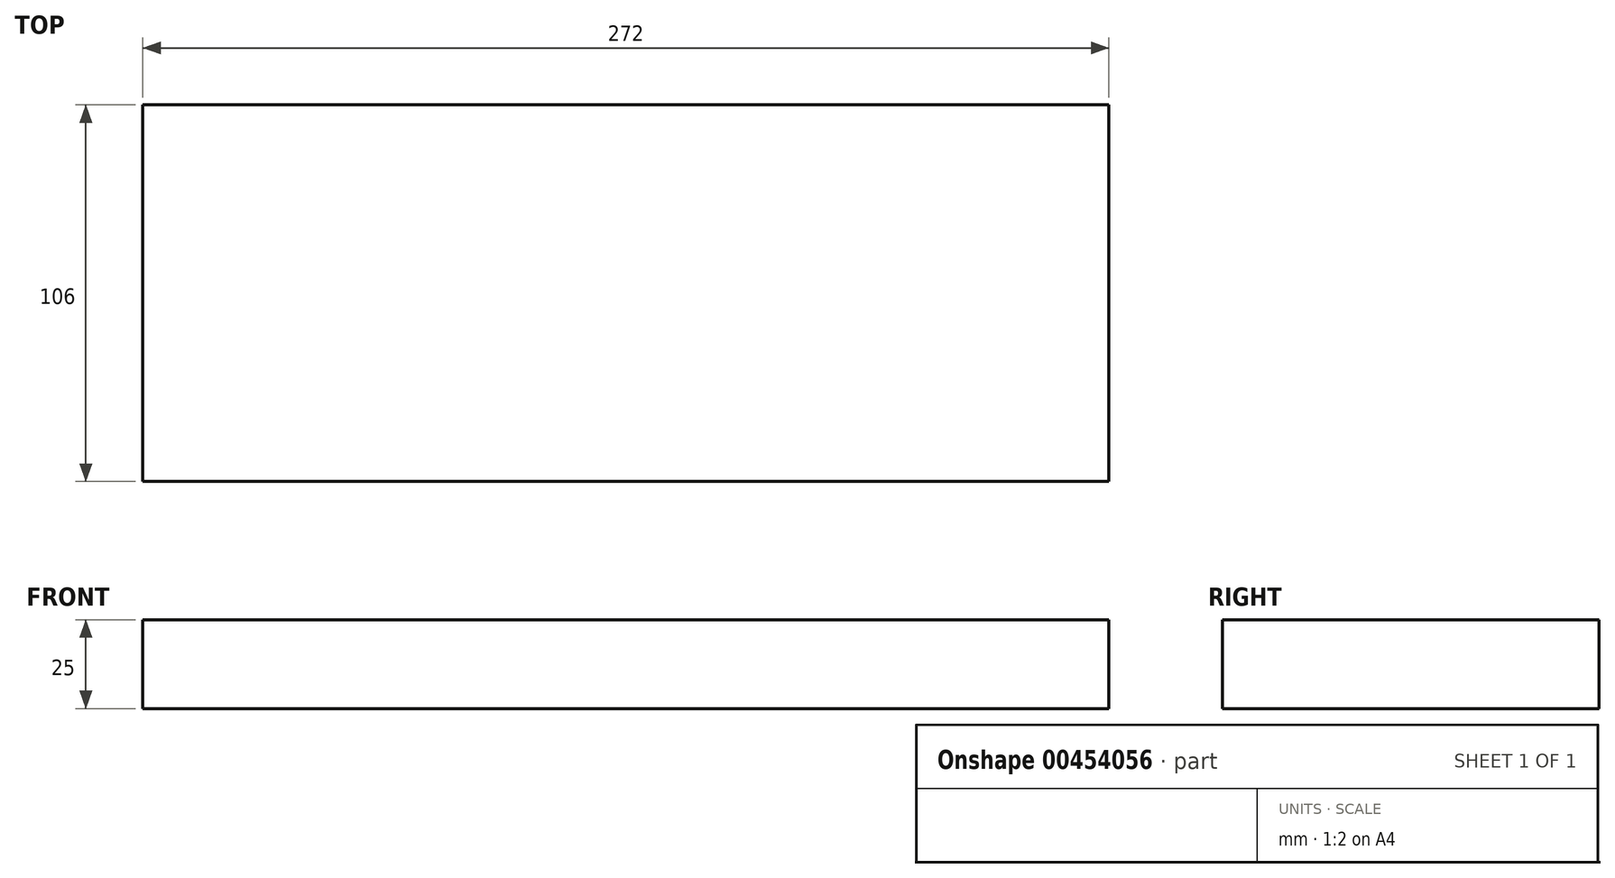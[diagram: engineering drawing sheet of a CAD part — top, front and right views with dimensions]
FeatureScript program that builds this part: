
annotation { "Feature Type Name" : "Feature", "Feature Type Description" : "" }
export const myFeature = defineFeature(function(context is Context, id is Id, definition is map)
    precondition{}
    {
        {
            var Q0;
            Q0=qCreatedBy(makeId("Top.planeOp"),FACE);
            var sketch = newSketch(context, id + "F0", { "sketchPlane" : qUnion([Q0])});
            skLineSegment(sketch, "E0.bottom", {"start": v(-96.67, -6.82) * mm, "end": v(175.33, -6.82) * mm});
            skLineSegment(sketch, "E0.top", {"start": v(-96.67, 99.18) * mm, "end": v(175.33, 99.18) * mm});
            skLineSegment(sketch, "E0.left", {"start": v(-96.67, -6.82) * mm, "end": v(-96.67, 99.18) * mm});
            skLineSegment(sketch, "E0.right", {"start": v(175.33, -6.82) * mm, "end": v(175.33, 99.18) * mm});
            skSolve(sketch);
        }
        {
            var Q0;
            Q0 = qSketchRegion(id + "F0", true);
            extrude(context, id + "F1", {"entities" : qUnion([Q0]), "depth" : 25 * mm, "offsetDistance" : 25 * mm});
        }
    });
